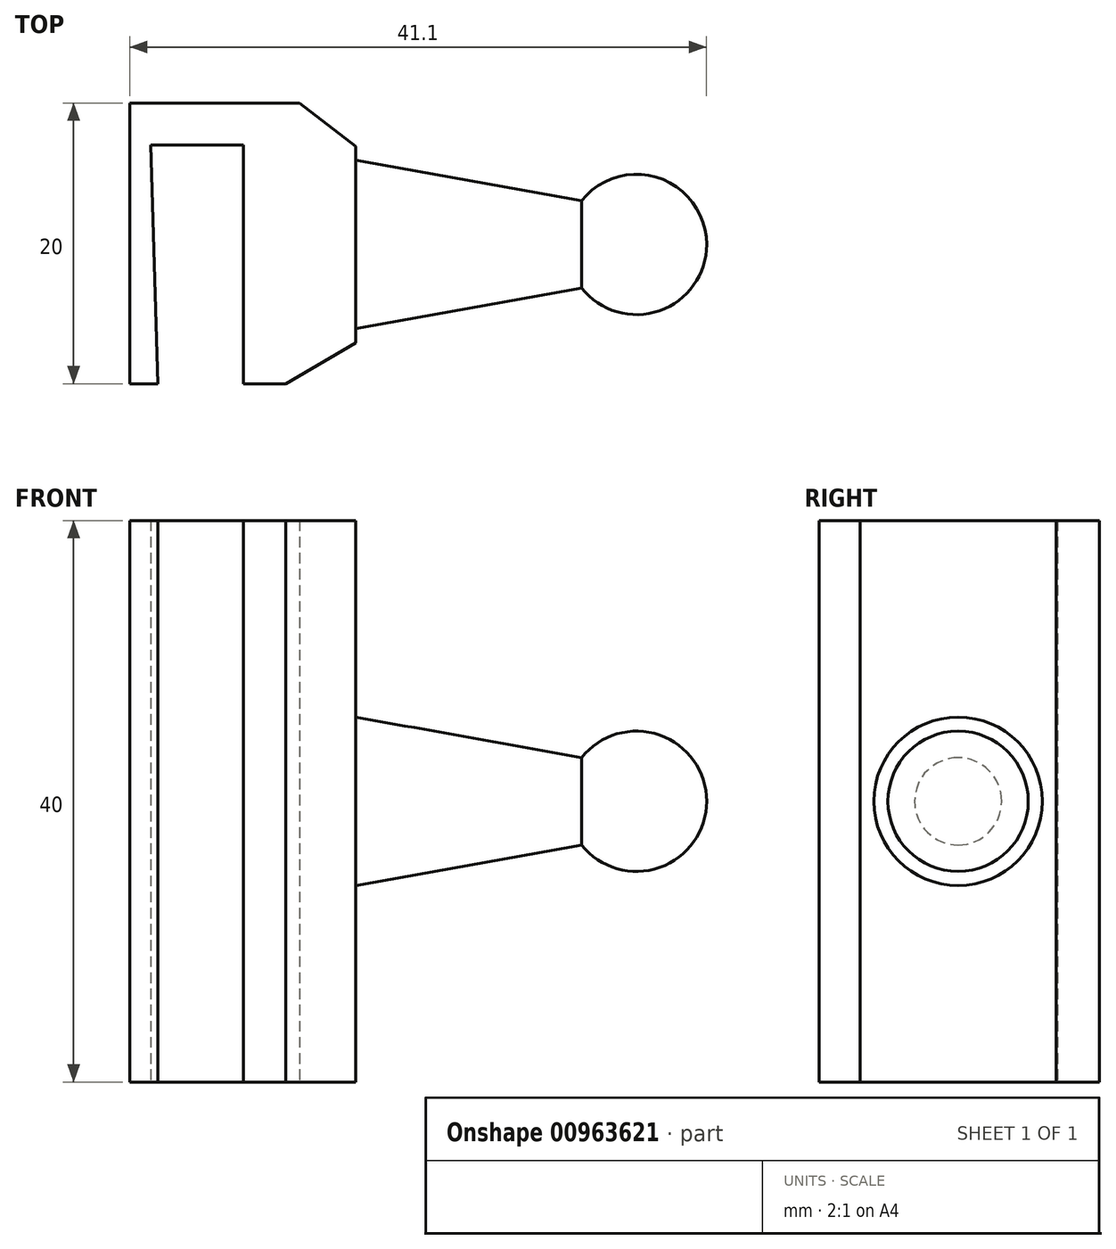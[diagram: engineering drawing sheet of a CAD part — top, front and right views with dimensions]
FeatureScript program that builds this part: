
annotation { "Feature Type Name" : "Feature", "Feature Type Description" : "" }
export const myFeature = defineFeature(function(context is Context, id is Id, definition is map)
    precondition{}
    {
        {
            var Q0;
            Q0=qCreatedBy(makeId("Top.planeOp"),FACE);
            var sketch = newSketch(context, id + "F0", { "sketchPlane" : qUnion([Q0])});
            skLineSegment(sketch, "E0", {"start": v(-33.94, -23.13) * mm, "end": v(-33.94, -3.13) * mm});
            skLineSegment(sketch, "E1", {"start": v(-33.94, -23.13) * mm, "end": v(-31.94, -23.13) * mm});
            skLineSegment(sketch, "E2", {"start": v(-31.94, -23.13) * mm, "end": v(-32.44, -6.13) * mm});
            skLineSegment(sketch, "E3", {"start": v(-33.94, -3.13) * mm, "end": v(-21.84, -3.13) * mm});
            skLineSegment(sketch, "E4", {"start": v(-25.84, -23.13) * mm, "end": v(-22.84, -23.13) * mm});
            skLineSegment(sketch, "E5", {"start": v(-25.84, -23.13) * mm, "end": v(-25.84, -6.13) * mm});
            skLineSegment(sketch, "E6", {"start": v(-25.84, -6.13) * mm, "end": v(-32.44, -6.13) * mm});
            skLineSegment(sketch, "E7", {"start": v(-21.84, -3.13) * mm, "end": v(-17.84, -6.2) * mm});
            skLineSegment(sketch, "E8", {"start": v(-17.84, -6.2) * mm, "end": v(-17.84, -20.2) * mm});
            skLineSegment(sketch, "E9", {"start": v(-17.84, -20.2) * mm, "end": v(-22.84, -23.13) * mm});
            skLineSegment(sketch, "E10", {"start": v(-17.84, -13.2) * mm, "end": v(-2.84, -13.2) * mm});
            skLineSegment(sketch, "E11", {"start": v(-2.84, -9.9) * mm, "end": v(-17.84, -7.2) * mm});
            skLineSegment(sketch, "E12", {"start": v(-2.84, -16.2) * mm, "end": v(-17.84, -19.2) * mm});
            skCircle(sketch, "E13", {"center": v(2.16, -13.2) * mm, "radius": 5 * mm});
            skLineSegment(sketch, "E14", {"start": v(-2.84, -9.9) * mm, "end": v(-1.76, -10.1) * mm});
            skLineSegment(sketch, "E15", {"start": v(-2.84, -16.2) * mm, "end": v(-1.96, -16.03) * mm});
            skLineSegment(sketch, "E16", {"start": v(-2.84, -13.2) * mm, "end": v(7.16, -13.2) * mm});
            skSolve(sketch);
        }
        {
            var Q0;
            Q0=makeQuery(id+"F0.imprint","IMPRINT",FACE,{"disambiguationData":[TD([[makeQuery(id+"F0.imprint","IMPRINT",EDGE,{"derivedFrom":sQuery(id+"F0.wireOp",EDGE,"E0")}),-1.0]])]});
            extrude(context, id + "F1", {"entities" : qUnion([Q0]), "endBound" : BoundingType.SYMMETRIC, "depth" : 40 * mm, "offsetDistance" : 25 * mm});
        }
        {
            var Q0;
            {var subQ1=sQuery(id+"F0.wireOp",EDGE,"E10");Q0=makeQuery(id+"F0.imprint","IMPRINT",FACE,{"disambiguationData":[TD([[makeQuery(id+"F0.imprint","IMPRINT",EDGE,{"derivedFrom":subQ1}),1.0]])]});}
            var Q1;
            Q1=sQuery(id+"F0.wireOp",EDGE,"E10");
            revolve(context, id + "F2", {"surfaceOperationType" : NewSurfaceOperationType.NEW, "entities" : qUnion([Q0]), "axis" : qUnion([Q1]), "revolveType" : RevolveType.FULL});
        }
        {
            var Q0;
            {var subQ2=sQuery(id+"F0.wireOp",EDGE,"E16");Q0=makeQuery(id+"F0.imprint","IMPRINT",FACE,{"disambiguationData":[TD([[makeQuery(id+"F0.imprint","IMPRINT",EDGE,{"derivedFrom":subQ2}),1.0]])]});}
            var Q1;
            Q1=sQuery(id+"F0.wireOp",EDGE,"E16");
            revolve(context, id + "F3", {"operationType" : NewBodyOperationType.ADD, "surfaceOperationType" : NewSurfaceOperationType.NEW, "entities" : qUnion([Q0]), "axis" : qUnion([Q1]), "revolveType" : RevolveType.FULL});
        }
    });
